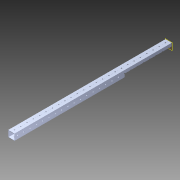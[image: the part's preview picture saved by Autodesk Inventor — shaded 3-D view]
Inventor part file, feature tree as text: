
AUTODESK INVENTOR PART (.ipt)
format: ipt  version: 2014 (Build 180170000, 170)  size: 1,339,904 bytes
history: native  units: in
note: dims shown in document units (in); Inventor stores cm internally (conversion verified against a paired STEP export)
features: extrude x3, sketch x3, pattern_circular x1, other x1, plane x1, imported_body x1
ambient origin geometry x8: Origin, YZ Plane, XZ Plane, XY Plane, X Axis, Y Axis, Z Axis, Center Point
bodies: Body1 (feature_tree)
feature tree (10):
  pattern_circular  "CirPattern2"
  other  "217-3426-STEP1"
  plane  "Work Plane1"
  extrude  "Extrusion1"  Depth=3937.0079in TaperAngle=0.0deg
  extrude  "Extrusion4"  Depth=0.5in
  extrude  "Extrusion5"  Depth=0.5in TaperAngle=0.0deg
  imported_body  "Base1"
  sketch  "Sketch1"  dims[d0=-25.0in d1=3937.0079in d2=0.0in]
  sketch  "Sketch5"  dims[d12=0.5in d13=7.5in]
  sketch  "Sketch6"  dims[d14=0.0787in d15=3.937in d16=0.0in d17=0.88in d19=0.35in d20=0.35in d22=0.5in d23=0.163in d24=0.163in d25=1.0in d26=0.0in]
